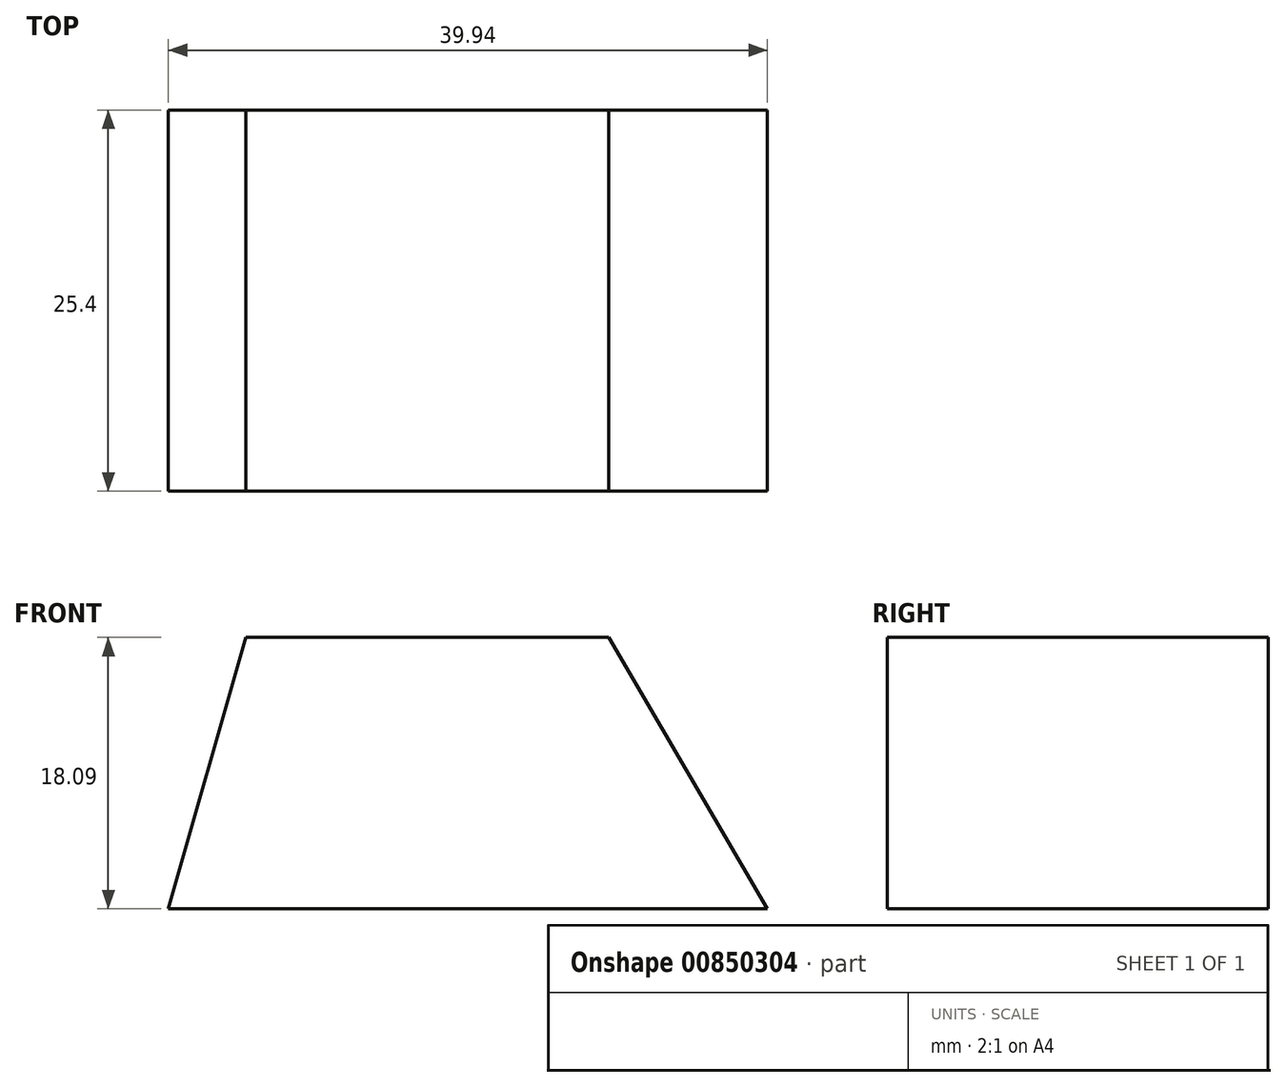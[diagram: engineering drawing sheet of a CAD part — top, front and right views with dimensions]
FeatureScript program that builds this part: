
annotation { "Feature Type Name" : "Feature", "Feature Type Description" : "" }
export const myFeature = defineFeature(function(context is Context, id is Id, definition is map)
    precondition{}
    {
        {
            var Q0;
            Q0=qCreatedBy(makeId("Front.planeOp"),FACE);
            var sketch = newSketch(context, id + "F0", { "sketchPlane" : qUnion([Q0])});
            skLineSegment(sketch, "E0", {"start": v(-50.76, 41.12) * mm, "end": v(-26.55, 41.12) * mm});
            skLineSegment(sketch, "E1", {"start": v(-26.55, 41.12) * mm, "end": v(-15.98, 23.03) * mm});
            skLineSegment(sketch, "E2", {"start": v(-55.92, 23.03) * mm, "end": v(-50.76, 41.12) * mm});
            skLineSegment(sketch, "E3", {"start": v(-55.92, 23.03) * mm, "end": v(-15.98, 23.03) * mm});
            skSolve(sketch);
        }
        {
            var Q0;
            Q0=qSketchRegion(id+"F0",true);
            extrude(context, id + "F1", {"entities" : qUnion([Q0]), "depth" : 25.4 * mm, "offsetDistance" : 25.4 * mm});
        }
    });
